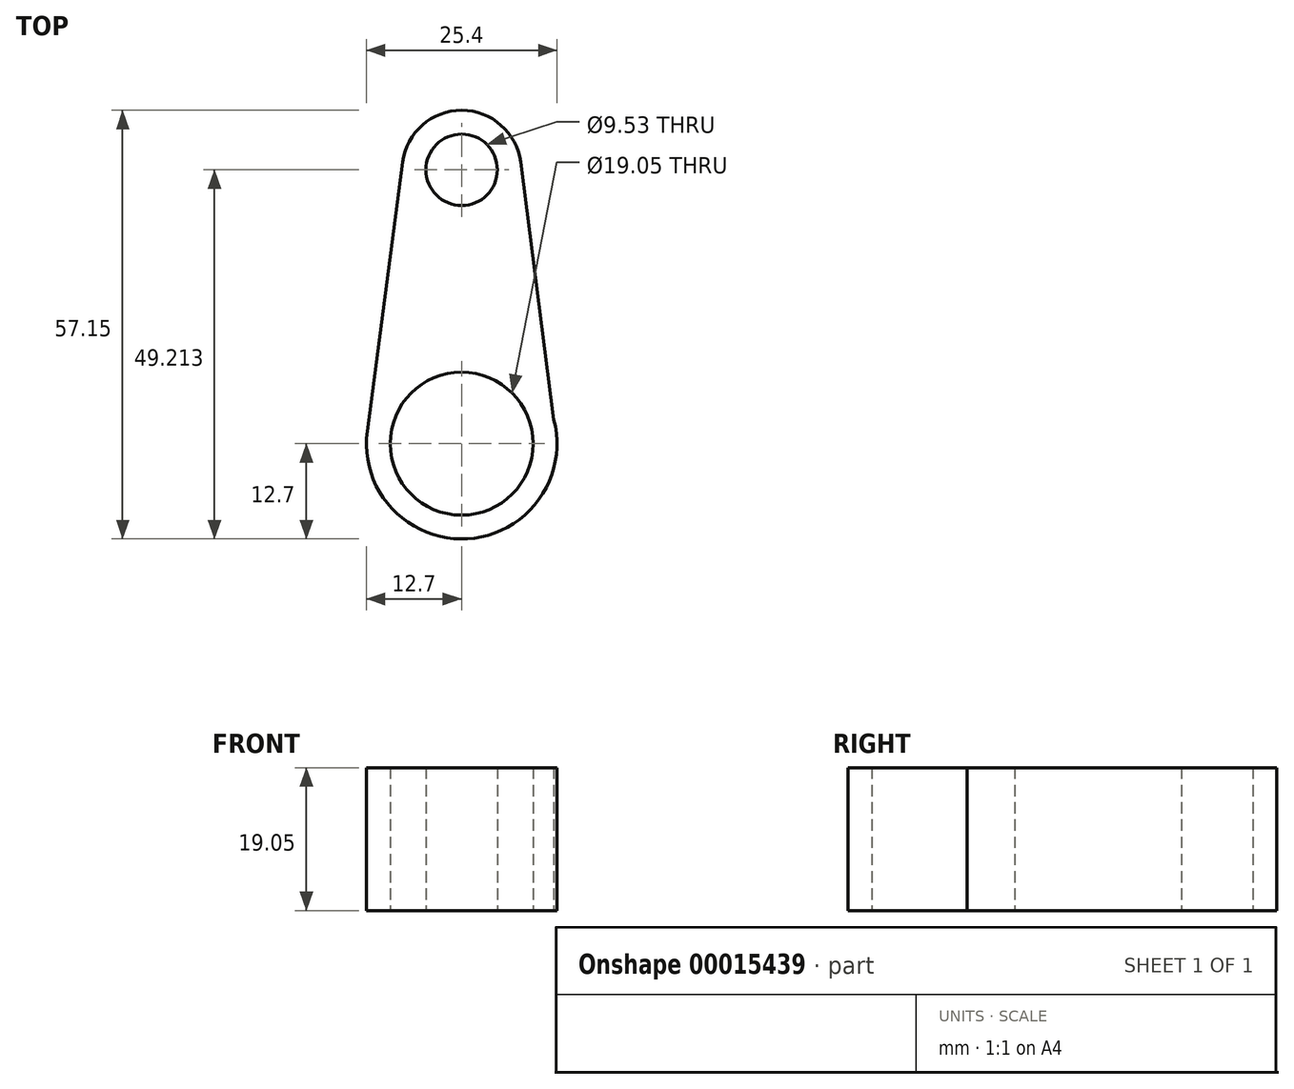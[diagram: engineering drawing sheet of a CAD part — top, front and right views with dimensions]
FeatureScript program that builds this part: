
annotation { "Feature Type Name" : "Feature", "Feature Type Description" : "" }
export const myFeature = defineFeature(function(context is Context, id is Id, definition is map)
    precondition{}
    {
        {
            var Q0;
            Q0=qCreatedBy(makeId("Top.planeOp"),FACE);
            var sketch = newSketch(context, id + "F0", { "sketchPlane" : qUnion([Q0])});
            skCircle(sketch, "E0", {"center": v(0, 0) * mm, "radius": 12.7 * mm});
            skCircle(sketch, "E1", {"center": v(0, 0) * mm, "radius": 9.53 * mm});
            skCircle(sketch, "E2", {"center": v(0, 36.51) * mm, "radius": 7.94 * mm});
            skCircle(sketch, "E3", {"center": v(0, 36.51) * mm, "radius": 4.76 * mm});
            skLineSegment(sketch, "E4", {"start": v(-7.87, 37.55) * mm, "end": v(-12.8, 0) * mm});
            skLineSegment(sketch, "E5", {"start": v(7.87, 37.53) * mm, "end": v(12.7, 0) * mm});
            skSolve(sketch);
        }
        {
            var Q0;
            Q0 = qSketchRegion(id + "F0", true);
            extrude(context, id + "F1", {"entities" : qUnion([Q0]), "depth" : 19.05 * mm});
        }
    });
